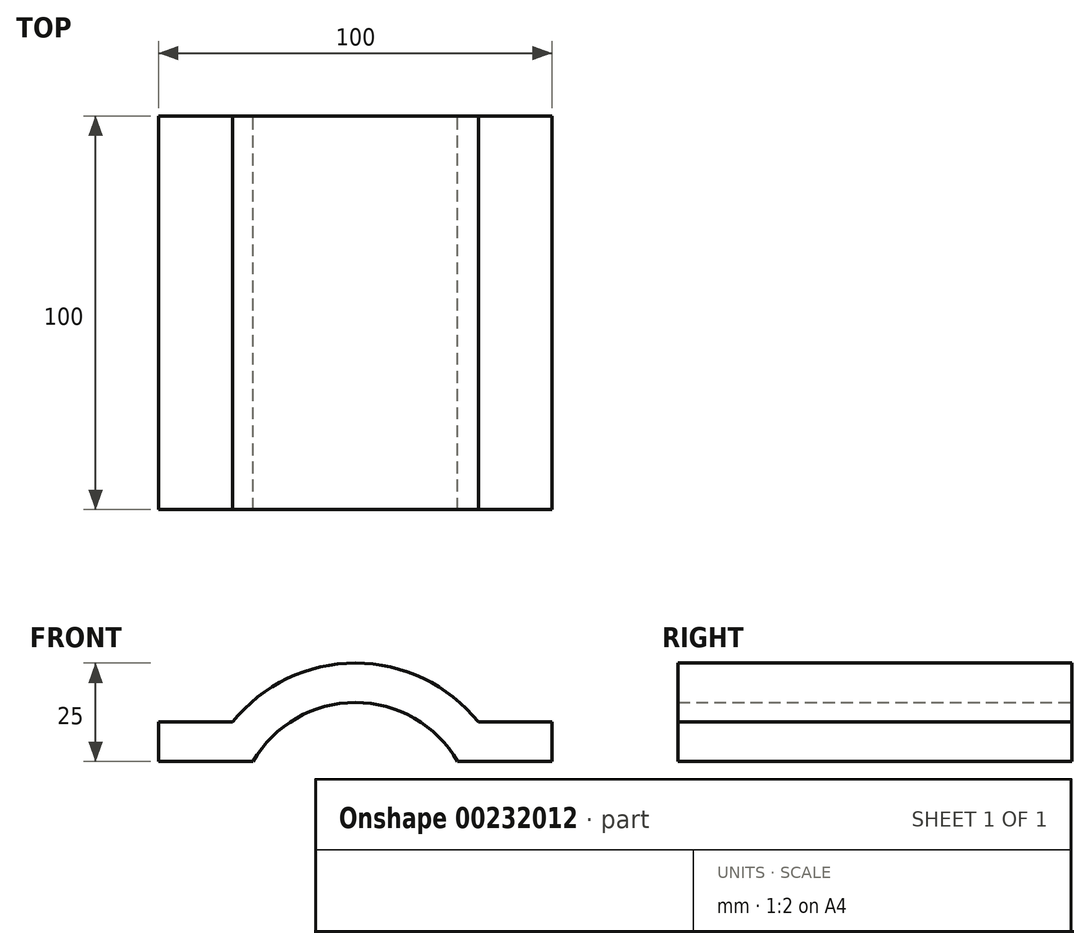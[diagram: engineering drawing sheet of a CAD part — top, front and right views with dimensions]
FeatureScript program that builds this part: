
annotation { "Feature Type Name" : "Feature", "Feature Type Description" : "" }
export const myFeature = defineFeature(function(context is Context, id is Id, definition is map)
    precondition{}
    {
        {
            var Q0;
            Q0=qCreatedBy(makeId("Front.planeOp"),FACE);
            var sketch = newSketch(context, id + "F0", { "sketchPlane" : qUnion([Q0])});
            skLineSegment(sketch, "E0", {"start": v(50, 25) * mm, "end": v(31.22, 25) * mm});
            skArc(sketch, "E1", {"start": v(31.22, 25) * mm, "mid": v(0, 40) * mm, "end": v(-31.22, 25) * mm});
            skLineSegment(sketch, "E2.MirrorCS", {"start": v(-50, 25) * mm, "end": v(-31.22, 25) * mm});
            skLineSegment(sketch, "E3.0", {"start": v(50, 15) * mm, "end": v(25.98, 15) * mm});
            skArc(sketch, "E3.1", {"start": v(25.98, 15) * mm, "mid": v(0, 30) * mm, "end": v(-25.98, 15) * mm});
            skLineSegment(sketch, "E3.2", {"start": v(-50, 15) * mm, "end": v(-25.98, 15) * mm});
            skLineSegment(sketch, "E4", {"start": v(-50, 25) * mm, "end": v(-50, 15) * mm});
            skLineSegment(sketch, "E5", {"start": v(50, 25) * mm, "end": v(50, 15) * mm});
            skSolve(sketch);
        }
        {
            var Q0;
            Q0=makeQuery(id+"F0.imprint","IMPRINT",FACE,{"disambiguationData":[TD([[makeQuery(id+"F0.imprint","IMPRINT",EDGE,{"derivedFrom":sQuery(id+"F0.wireOp",EDGE,"E0")}),1.0]])]});
            extrude(context, id + "F1", {"entities" : qUnion([Q0]), "depth" : 100 * mm});
        }
    });
